# Revit family: Schutzkappen 27-18 bis 36-40
name_source: partatom
category: HLS-Bauteile
revit_build: Autodesk Revit 2017 (Build: 20190507_1515(x64)
units: mm (PartAtom-declared; Revit-internal decimal feet)

## family parameters
Arbeitsebenenbasiert = Ja
Beim Laden mit Abzugskörper schneiden = Nein
Bemaßung runder Anschluss = Durchmesser verwenden
Gemeinsam genutzt = Ja
Immer vertikal = Nein
Raumberechnungspunkt = Nein
Teiletyp = Normal

## types (3) — shared parameters
B2 = 4 mm  [stored 0.0131234 ft]
BP = 4 mm  [stored 0.0131234 ft]
Fabrikat = MEFA
Farbe = schwarz
Firma = MEFA Befestigungs- und Montagesysteme GmbH
L1 = 5 mm  [stored 0.0164042 ft]
Material = Kunststoff
Materialname = PE
Mengeneinheit = St
Vorgabe-Ansicht = 1219 mm
vpe = 50 St

## per-type parameters (varying)
| type | Artikelnummer | B | B1 | C | D | EAN | Gewicht | H1 | H2 | Kurztext1 | Kurztext2 | L2 | Profiltyp |
| Schutzkappe 27- 18 | 0809032 | 27 mm  [stored 0.0885827 ft] | 18 mm  [stored 0.0590551 ft] | 19 mm  [stored 0.062336 ft] | 10 mm  [stored 0.0328084 ft] | 4250928419316 | 0.00 kg | 4 mm  [stored 0.0131234 ft] | 7 mm  [stored 0.0229659 ft] | Endkappe C-Profil 27 | für Profil 27/18 PE Schwarz | 20 mm  [stored 0.0656168 ft] | 27/18 |
| Schutzkappe 35- 21 | 0809012 | 35 mm  [stored 0.114829 ft] | 21 mm  [stored 0.0688976 ft] | 27 mm  [stored 0.0885827 ft] | 13 mm  [stored 0.0426509 ft] | 4250928419309 | 0.01 kg | 8 mm  [stored 0.0262467 ft] | 9 mm  [stored 0.0295276 ft] | Endkappe C-Profil 35 | für Profil 35/21 PE Schwarz | 20 mm  [stored 0.0656168 ft] | 35/21 |
| Schutzkappe 36- 40 | 0809045 | 36 mm  [stored 0.11811 ft] | 40 mm  [stored 0.131234 ft] | 28 mm  [stored 0.0918635 ft] | 32 mm  [stored 0.104987 ft] | 4250928449863 | 0.01 kg | 9 mm  [stored 0.0295276 ft] | 18 mm  [stored 0.0590551 ft] | Endkappe C-Profil 36 | für Profil 36/40 PE Schwarz | 17 mm | 36/40 |

note: [stored X ft] marks values corroborated as IEEE doubles in the binary element streams (Revit-internal decimal feet)
